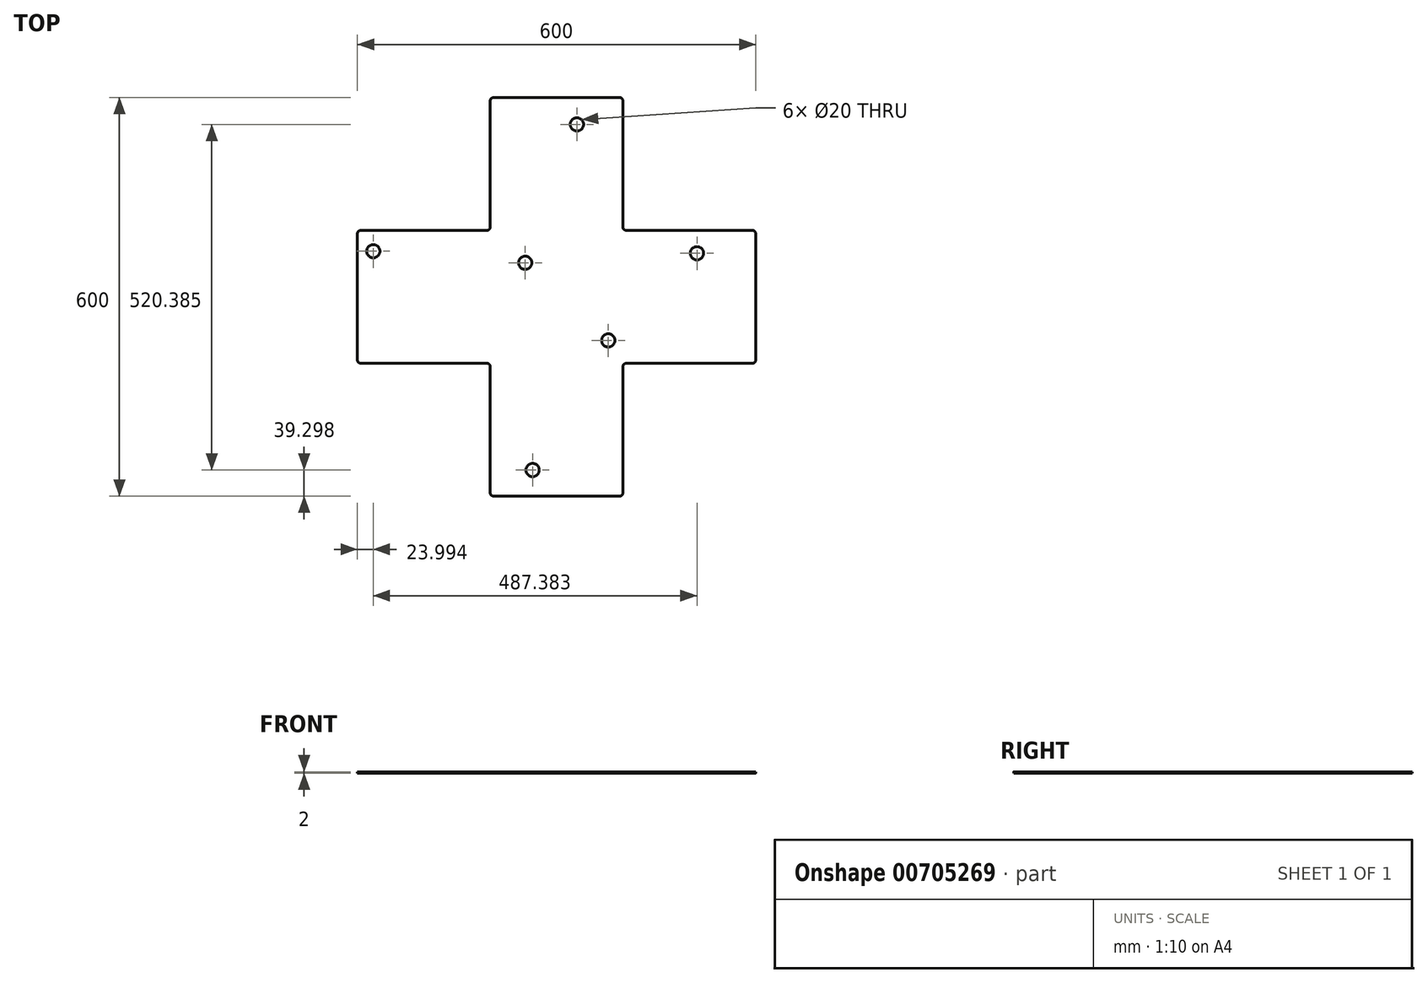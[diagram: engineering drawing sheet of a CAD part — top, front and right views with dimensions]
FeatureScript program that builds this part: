
annotation { "Feature Type Name" : "Feature", "Feature Type Description" : "" }
export const myFeature = defineFeature(function(context is Context, id is Id, definition is map)
    precondition{}
    {
        {
            var Q0;
            Q0=qCreatedBy(makeId("Top.planeOp"),FACE);
            var sketch = newSketch(context, id + "F0", { "sketchPlane" : qUnion([Q0])});
            skLineSegment(sketch, "E0", {"start": v(-300, -100) * mm, "end": v(-300, 100) * mm});
            skLineSegment(sketch, "E1", {"start": v(-300, 100) * mm, "end": v(-100, 100) * mm});
            skLineSegment(sketch, "E2", {"start": v(-100, 100) * mm, "end": v(-100, 300) * mm});
            skLineSegment(sketch, "E3", {"start": v(-100, 300) * mm, "end": v(100, 300) * mm});
            skLineSegment(sketch, "E4", {"start": v(100, 300) * mm, "end": v(100, 100) * mm});
            skLineSegment(sketch, "E5", {"start": v(100, 100) * mm, "end": v(300, 100) * mm});
            skLineSegment(sketch, "E6", {"start": v(300, 100) * mm, "end": v(300, -100) * mm});
            skLineSegment(sketch, "E7", {"start": v(300, -100) * mm, "end": v(100, -100) * mm});
            skLineSegment(sketch, "E8", {"start": v(100, -100) * mm, "end": v(100, -300) * mm});
            skLineSegment(sketch, "E9", {"start": v(100, -300) * mm, "end": v(-100, -300) * mm});
            skLineSegment(sketch, "E10", {"start": v(-100, -300) * mm, "end": v(-100, -100) * mm});
            skLineSegment(sketch, "E11", {"start": v(-100, -100) * mm, "end": v(-300, -100) * mm});
            skSolve(sketch);
        }
        {
            var Q0;
            Q0=makeQuery(id+"F0.imprint","IMPRINT",FACE,{"disambiguationData":[TD([[makeQuery(id+"F0.imprint","IMPRINT",EDGE,{"derivedFrom":sQuery(id+"F0.wireOp",EDGE,"E0")}),-1.0]])]});
            extrude(context, id + "F1", {"entities" : qUnion([Q0]), "depth" : 2 * mm, "offsetDistance" : 25 * mm});
        }
        {
            var Q0;
            Q0=makeQuery(id+"F1.opExtrude","SWEPT_EDGE",EDGE,{"disambiguationData":[OSD([sQuery(id+"F0.wireOp",EDGE,"E0"),sQuery(id+"F0.wireOp",EDGE,"E11")])]});
            var Q1;
            Q1=makeQuery(id+"F1.opExtrude","SWEPT_EDGE",EDGE,{"disambiguationData":[OSD([sQuery(id+"F0.wireOp",EDGE,"E10"),sQuery(id+"F0.wireOp",EDGE,"E11")])]});
            var Q2;
            Q2=makeQuery(id+"F1.opExtrude","SWEPT_EDGE",EDGE,{"disambiguationData":[OSD([sQuery(id+"F0.wireOp",EDGE,"E9"),sQuery(id+"F0.wireOp",EDGE,"E10")])]});
            var Q3;
            Q3=makeQuery(id+"F1.opExtrude","SWEPT_EDGE",EDGE,{"disambiguationData":[OSD([sQuery(id+"F0.wireOp",EDGE,"E8"),sQuery(id+"F0.wireOp",EDGE,"E9")])]});
            var Q4;
            Q4=makeQuery(id+"F1.opExtrude","SWEPT_EDGE",EDGE,{"disambiguationData":[OSD([sQuery(id+"F0.wireOp",EDGE,"E0"),sQuery(id+"F0.wireOp",EDGE,"E1")])]});
            var Q5;
            Q5=makeQuery(id+"F1.opExtrude","SWEPT_EDGE",EDGE,{"disambiguationData":[OSD([sQuery(id+"F0.wireOp",EDGE,"E2"),sQuery(id+"F0.wireOp",EDGE,"E3")])]});
            var Q6;
            Q6=makeQuery(id+"F1.opExtrude","SWEPT_EDGE",EDGE,{"disambiguationData":[OSD([sQuery(id+"F0.wireOp",EDGE,"E3"),sQuery(id+"F0.wireOp",EDGE,"E4")])]});
            var Q7;
            Q7=makeQuery(id+"F1.opExtrude","SWEPT_EDGE",EDGE,{"disambiguationData":[OSD([sQuery(id+"F0.wireOp",EDGE,"E4"),sQuery(id+"F0.wireOp",EDGE,"E5")])]});
            var Q8;
            Q8=makeQuery(id+"F1.opExtrude","SWEPT_EDGE",EDGE,{"disambiguationData":[OSD([sQuery(id+"F0.wireOp",EDGE,"E5"),sQuery(id+"F0.wireOp",EDGE,"E6")])]});
            var Q9;
            Q9=makeQuery(id+"F1.opExtrude","SWEPT_EDGE",EDGE,{"disambiguationData":[OSD([sQuery(id+"F0.wireOp",EDGE,"E6"),sQuery(id+"F0.wireOp",EDGE,"E7")])]});
            var Q10;
            Q10=makeQuery(id+"F1.opExtrude","SWEPT_EDGE",EDGE,{"disambiguationData":[OSD([sQuery(id+"F0.wireOp",EDGE,"E1"),sQuery(id+"F0.wireOp",EDGE,"E2")])]});
            var Q11;
            Q11=makeQuery(id+"F1.opExtrude","SWEPT_EDGE",EDGE,{"disambiguationData":[OSD([sQuery(id+"F0.wireOp",EDGE,"E7"),sQuery(id+"F0.wireOp",EDGE,"E8")])]});
            fillet(context, id + "F2", {"entities" : qUnion([Q0, Q1, Q2, Q3, Q4, Q5, Q6, Q7, Q8, Q9, Q10, Q11]), "radius" : 5 * mm, "tangentPropagation" : true, "allowEdgeOverflow" : false});
        }
        {
            var Q0;
            Q0=qCreatedBy(makeId("Top.planeOp"),FACE);
            var sketch = newSketch(context, id + "F3", { "sketchPlane" : qUnion([Q0])});
            skPoint(sketch, "E12", {"position": v(-276, 68.7) * mm});
            skPoint(sketch, "E13", {"position": v(-47.22, 51.34) * mm});
            skPoint(sketch, "E14", {"position": v(77.83, -65.6) * mm});
            skPoint(sketch, "E15", {"position": v(-36.12, -260.7) * mm});
            skPoint(sketch, "E16", {"position": v(211.38, 65.62) * mm});
            skPoint(sketch, "E17", {"position": v(30.64, 259.68) * mm});
            skSolve(sketch);
        }
        {
            var Q0;
            Q0=sQuery(id+"F3.wireOp",VERTEX,"E12");
            var Q1;
            Q1=sQuery(id+"F3.wireOp",VERTEX,"E13");
            var Q2;
            Q2=sQuery(id+"F3.wireOp",VERTEX,"E14");
            var Q3;
            Q3=sQuery(id+"F3.wireOp",VERTEX,"E15");
            var Q4;
            Q4=sQuery(id+"F3.wireOp",VERTEX,"E16");
            var Q5;
            Q5=sQuery(id+"F3.wireOp",VERTEX,"E17");
            var Q6;
            Q6=makeQuery(id+"F1.opExtrude","SWEPT_BODY",BODY,{"disambiguationData":[OSD([sQuery(id+"F0.wireOp",EDGE,"E0"),sQuery(id+"F0.wireOp",EDGE,"E1"),sQuery(id+"F0.wireOp",EDGE,"E2"),sQuery(id+"F0.wireOp",EDGE,"E3"),sQuery(id+"F0.wireOp",EDGE,"E4"),sQuery(id+"F0.wireOp",EDGE,"E5"),sQuery(id+"F0.wireOp",EDGE,"E6"),sQuery(id+"F0.wireOp",EDGE,"E7"),sQuery(id+"F0.wireOp",EDGE,"E8"),sQuery(id+"F0.wireOp",EDGE,"E9"),sQuery(id+"F0.wireOp",EDGE,"E10"),sQuery(id+"F0.wireOp",EDGE,"E11")])]});
            hole(context, id + "F4", {"style" : HoleStyle.SIMPLE, "endStyle" : HoleEndStyle.BLIND, "oppositeDirection" : true, "holeDiameter" : 20 * mm, "majorDiameter" : 5 * mm, "holeDepth" : 50 * mm, "isTappedThrough" : true, "tappedDepth" : 12 * mm, "tapClearance" : 3, "startFromSketch" : true, "locations" : qUnion([Q0, Q1, Q2, Q3, Q4, Q5]), "scope" : qUnion([Q6])});
        }
    });
